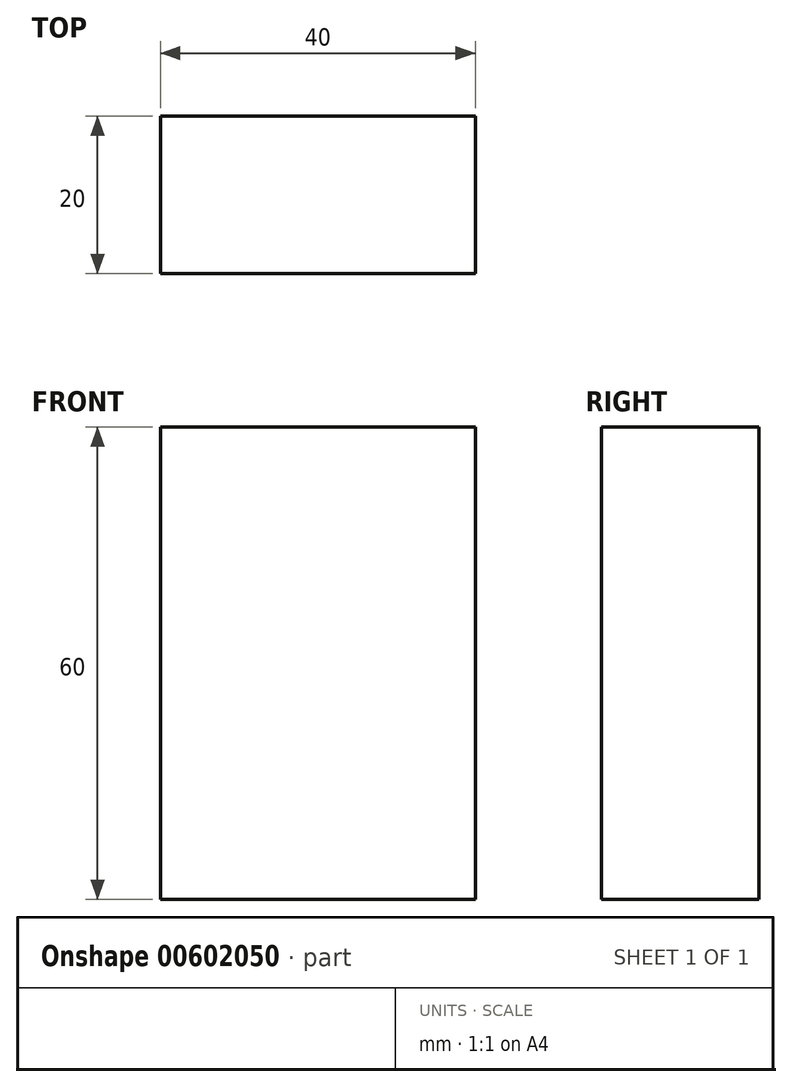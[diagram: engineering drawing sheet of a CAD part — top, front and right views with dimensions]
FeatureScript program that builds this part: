
annotation { "Feature Type Name" : "Feature", "Feature Type Description" : "" }
export const myFeature = defineFeature(function(context is Context, id is Id, definition is map)
    precondition{}
    {
        {
            var Q0;
            Q0=qCreatedBy(makeId("Front.planeOp"),FACE);
            var sketch = newSketch(context, id + "F0", { "sketchPlane" : qUnion([Q0])});
            skLineSegment(sketch, "E0", {"start": v(-51.65, 48.6) * mm, "end": v(-11.65, 48.6) * mm});
            skLineSegment(sketch, "E1", {"start": v(-11.65, 48.6) * mm, "end": v(-11.65, -11.4) * mm});
            skLineSegment(sketch, "E2", {"start": v(-51.65, 48.6) * mm, "end": v(-51.65, -11.4) * mm});
            skLineSegment(sketch, "E3", {"start": v(-51.65, -11.4) * mm, "end": v(-11.65, -11.4) * mm});
            skSolve(sketch);
        }
        {
            var Q0;
            Q0 = qSketchRegion(id + "F0", true);
            extrude(context, id + "F1", {"entities" : qUnion([Q0]), "depth" : 20 * mm, "offsetDistance" : 25 * mm});
        }
    });
